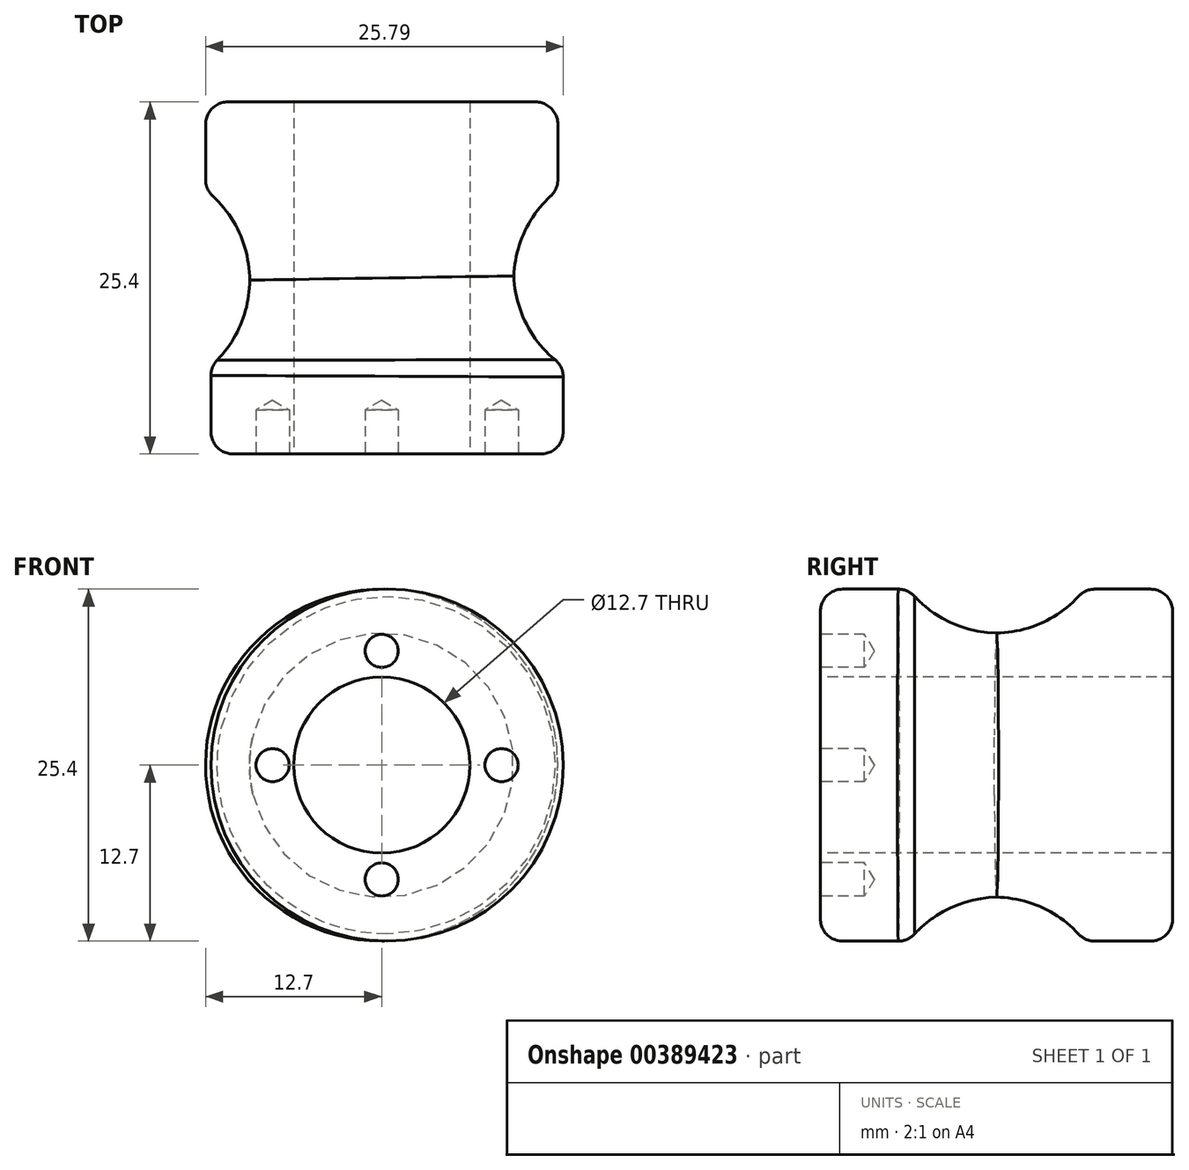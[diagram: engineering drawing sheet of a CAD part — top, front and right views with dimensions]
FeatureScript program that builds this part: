
annotation { "Feature Type Name" : "Feature", "Feature Type Description" : "" }
export const myFeature = defineFeature(function(context is Context, id is Id, definition is map)
    precondition{}
    {
        {
            var Q0;
            Q0=qCreatedBy(makeId("Front.planeOp"),FACE);
            var sketch = newSketch(context, id + "F0", { "sketchPlane" : qUnion([Q0])});
            skCircle(sketch, "E0", {"center": v(0.39, 0) * mm, "radius": 12.7 * mm});
            skSolve(sketch);
        }
        {
            var Q0;
            Q0 = qSketchRegion(id + "F0", true);
            extrude(context, id + "F1", {"entities" : qUnion([Q0]), "depth" : 6.35 * mm});
        }
        {
            var Q0;
            Q0=makeQuery(id+"F1.opExtrude","CAP_FACE",FACE,{"disambiguationData":[OSD([sQuery(id+"F0.wireOp",EDGE,"E0")])],"isStart":true});
            var sketch = newSketch(context, id + "F2", { "sketchPlane" : qUnion([Q0])});
            skCircle(sketch, "E1", {"center": v(0, 0) * mm, "radius": 9.53 * mm});
            skSolve(sketch);
        }
        {
            var Q0;
            Q0 = qSketchRegion(id + "F2", true);
            extrude(context, id + "F3", {"entities" : qUnion([Q0]), "operationType" : NewBodyOperationType.ADD, "depth" : 12.7 * mm});
        }
        {
            var Q0;
            Q0=makeQuery(id+"F3.opExtrude","CAP_FACE",FACE,{"disambiguationData":[OSD([sQuery(id+"F2.wireOp",EDGE,"E1")])],"isStart":false});
            var sketch = newSketch(context, id + "F4", { "sketchPlane" : qUnion([Q0])});
            skCircle(sketch, "E2", {"center": v(0, 0) * mm, "radius": 12.7 * mm});
            skSolve(sketch);
        }
        {
            var Q0;
            Q0 = qSketchRegion(id + "F4", true);
            extrude(context, id + "F5", {"entities" : qUnion([Q0]), "operationType" : NewBodyOperationType.ADD, "depth" : 6.35 * mm});
        }
        {
            var Q0;
            Q0=makeQuery(id+"F1.opExtrude","CAP_FACE",FACE,{"disambiguationData":[OSD([sQuery(id+"F0.wireOp",EDGE,"E0")])],"isStart":false});
            var sketch = newSketch(context, id + "F6", { "sketchPlane" : qUnion([Q0])});
            skPoint(sketch, "E3", {"position": v(0, 8.25) * mm});
            skPoint(sketch, "E4", {"position": v(8.64, 0) * mm});
            skPoint(sketch, "E5", {"position": v(0, -8.25) * mm});
            skPoint(sketch, "E6", {"position": v(-7.87, 0) * mm});
            skSolve(sketch);
        }
        {
            var Q0;
            Q0=sQuery(id+"F6.wireOp",VERTEX,"E3");
            var Q1;
            Q1=sQuery(id+"F6.wireOp",VERTEX,"E6");
            var Q2;
            Q2=sQuery(id+"F6.wireOp",VERTEX,"E5");
            var Q3;
            Q3=sQuery(id+"F6.wireOp",VERTEX,"E4");
            var Q4;
            Q4=makeQuery(id+"F1.opExtrude","SWEPT_BODY",BODY,{"disambiguationData":[OSD([sQuery(id+"F0.wireOp",EDGE,"E0")])]});
            hole(context, id + "F7", {"style" : HoleStyle.SIMPLE, "endStyle" : HoleEndStyle.BLIND, "holeDiameter" : 2.4 * mm, "holeDepth" : 3.17 * mm, "isTappedThrough" : true, "tappedDepth" : 12.7 * mm, "tapClearance" : 3, "locations" : qUnion([Q0, Q1, Q2, Q3]), "scope" : qUnion([Q4])});
        }
        {
            var Q0;
            Q0=makeQuery(id+"F1.opExtrude","CAP_FACE",FACE,{"disambiguationData":[OSD([sQuery(id+"F0.wireOp",EDGE,"E0")])],"isStart":false});
            var sketch = newSketch(context, id + "F8", { "sketchPlane" : qUnion([Q0])});
            skPoint(sketch, "E7", {"position": v(0, 0) * mm});
            skSolve(sketch);
        }
        {
            var Q0;
            Q0=sQuery(id+"F8.wireOp",VERTEX,"E7");
            var Q1;
            Q1=makeQuery(id+"F1.opExtrude","SWEPT_BODY",BODY,{"disambiguationData":[OSD([sQuery(id+"F0.wireOp",EDGE,"E0")])]});
            hole(context, id + "F9", {"style" : HoleStyle.SIMPLE, "endStyle" : HoleEndStyle.THROUGH, "holeDiameter" : 12.7 * mm, "isTappedThrough" : true, "tappedDepth" : 12.7 * mm, "tapClearance" : 3, "locations" : qUnion([Q0]), "scope" : qUnion([Q1])});
        }
        {
            var Q0;
            Q0=makeQuery(id+"F3.opExtrude","SWEPT_FACE",FACE,{"disambiguationData":[OSD([sQuery(id+"F2.wireOp",EDGE,"E1")])]});
            fillet(context, id + "F10", {"entities" : qUnion([Q0]), "radius" : 8.25 * mm, "tangentPropagation" : true, "allowEdgeOverflow" : false});
        }
        {
            var Q0;
            Q0=makeQuery(id+"F5.opExtrude","CAP_EDGE",EDGE,{"disambiguationData":[OSD([sQuery(id+"F4.wireOp",EDGE,"E2")])],"isStart":false});
            var Q1;
            Q1=makeQuery(id+"F1.opExtrude","CAP_EDGE",EDGE,{"disambiguationData":[OSD([sQuery(id+"F0.wireOp",EDGE,"E0")])],"isStart":false});
            var Q2;
            Q2=makeQuery(id+"F1.opExtrude","SWEPT_FACE",FACE,{"disambiguationData":[OSD([sQuery(id+"F0.wireOp",EDGE,"E0")])]});
            var Q3;
            Q3=makeQuery(id+"F5.opExtrude","SWEPT_FACE",FACE,{"disambiguationData":[OSD([sQuery(id+"F4.wireOp",EDGE,"E2")])]});
            fillet(context, id + "F11", {"entities" : qUnion([Q0, Q1, Q2, Q3]), "radius" : 1.6 * mm, "tangentPropagation" : true, "allowEdgeOverflow" : false});
        }
    });
